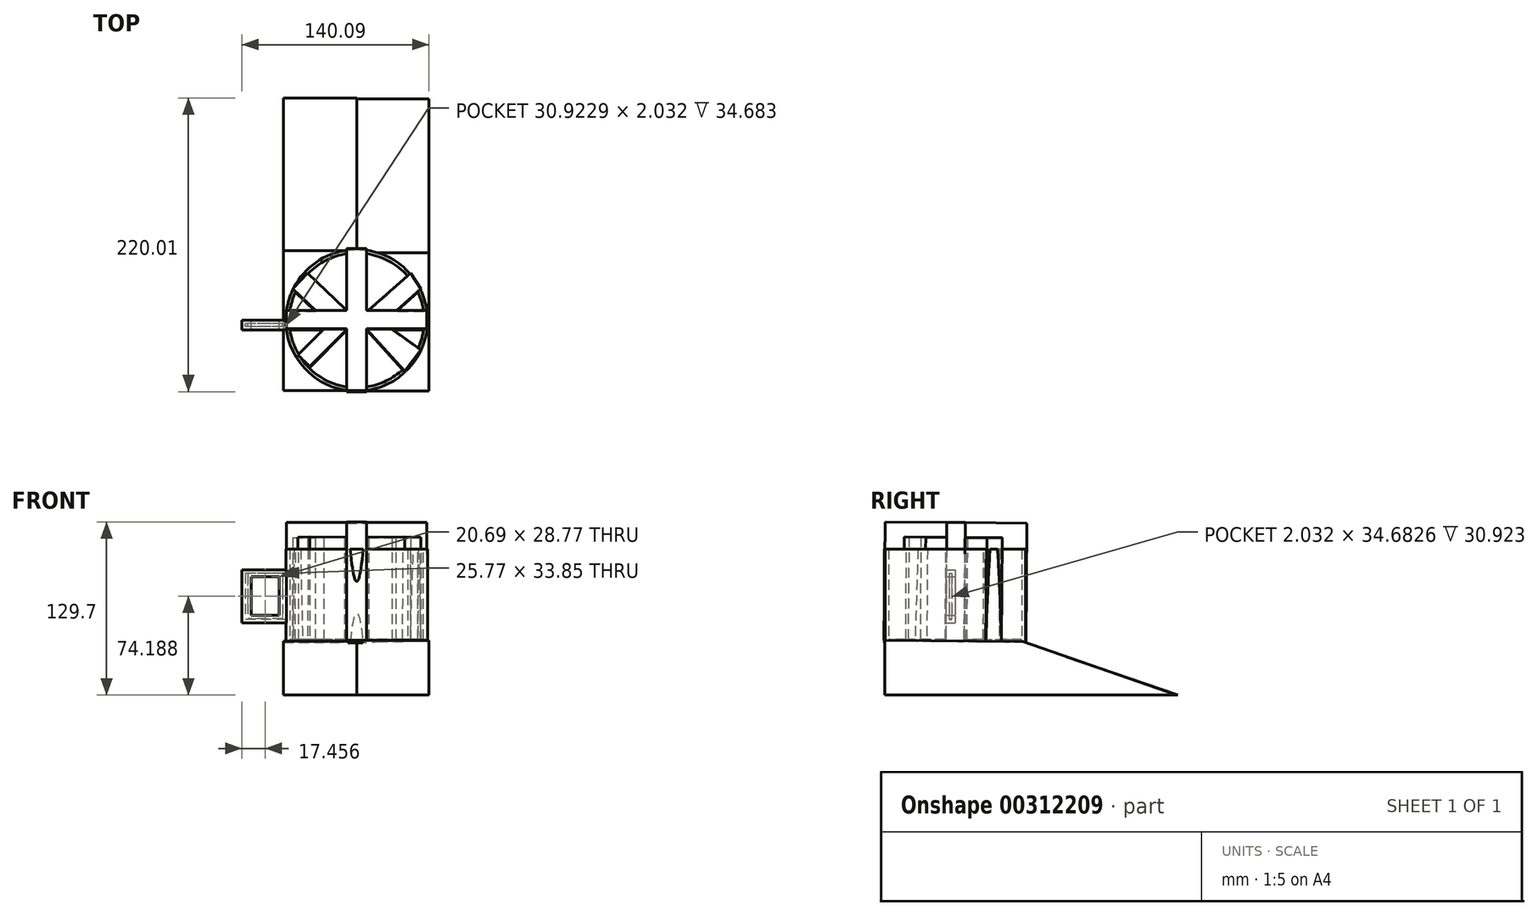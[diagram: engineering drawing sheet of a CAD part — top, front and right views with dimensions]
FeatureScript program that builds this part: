
annotation { "Feature Type Name" : "Feature", "Feature Type Description" : "" }
export const myFeature = defineFeature(function(context is Context, id is Id, definition is map)
    precondition{}
    {
        {
            var Q0;
            Q0=qCreatedBy(makeId("Front.planeOp"),FACE);
            var sketch = newSketch(context, id + "F0", { "sketchPlane" : qUnion([Q0])});
            skLineSegment(sketch, "E0.bottom", {"start": v(0, -34.1) * mm, "end": v(-53.02, -34.1) * mm});
            skLineSegment(sketch, "E0.top", {"start": v(0, 36.04) * mm, "end": v(-53.02, 36.04) * mm});
            skLineSegment(sketch, "E0.left", {"start": v(0, -34.1) * mm, "end": v(0, 36.04) * mm});
            skLineSegment(sketch, "E0.right", {"start": v(-53.02, -34.1) * mm, "end": v(-53.02, 36.04) * mm});
            skSolve(sketch);
        }
        {
            var Q0;
            Q0 = qSketchRegion(id + "F0", true);
            var Q1;
            Q1=sQuery(id+"F0.wireOp",EDGE,"E0.left");
            revolve(context, id + "F1", {"entities" : qUnion([Q0]), "axis" : qUnion([Q1]), "revolveType" : RevolveType.FULL});
        }
        {
            var Q0;
            Q0=qCreatedBy(makeId("Front.planeOp"),FACE);
            var sketch = newSketch(context, id + "F2", { "sketchPlane" : qUnion([Q0])});
            skLineSegment(sketch, "E1.bottom", {"start": v(-52.05, 20.53) * mm, "end": v(-86, 20.53) * mm});
            skLineSegment(sketch, "E1.top", {"start": v(-52.05, -19.24) * mm, "end": v(-86, -19.24) * mm});
            skLineSegment(sketch, "E1.left", {"start": v(-52.05, 20.53) * mm, "end": v(-52.05, -19.24) * mm});
            skLineSegment(sketch, "E1.right", {"start": v(-86, 20.53) * mm, "end": v(-86, -19.24) * mm});
            skLineSegment(sketch, "E2.bottom", {"start": v(-58.19, 15.35) * mm, "end": v(-78.88, 15.35) * mm});
            skLineSegment(sketch, "E2.top", {"start": v(-58.19, -13.42) * mm, "end": v(-78.88, -13.42) * mm});
            skLineSegment(sketch, "E2.left", {"start": v(-58.19, 15.35) * mm, "end": v(-58.19, -13.42) * mm});
            skLineSegment(sketch, "E2.right", {"start": v(-78.88, 15.35) * mm, "end": v(-78.88, -13.42) * mm});
            skSolve(sketch);
        }
        {
            var Q0;
            Q0=makeQuery(id+"F2.imprint","IMPRINT",FACE,{"disambiguationData":[TD([[makeQuery(id+"F2.imprint","IMPRINT",EDGE,{"derivedFrom":sQuery(id+"F2.wireOp",EDGE,"E1.bottom")}),1.0]])]});
            extrude(context, id + "F3", {"entities" : qUnion([Q0]), "operationType" : NewBodyOperationType.ADD, "depth" : 7.11 * mm});
        }
        {
            var Q0;
            Q0=makeQuery(id+"F1.opRevolve","SWEPT_FACE",FACE,{"disambiguationData":[OSD([sQuery(id+"F0.wireOp",EDGE,"E0.top")])]});
            shell(context, id + "F4", {"entities" : qUnion([Q0]), "thickness" : 2.54 * mm});
        }
        {
            var Q0;
            Q0=qCreatedBy(makeId("Right.planeOp"),FACE);
            var sketch = newSketch(context, id + "F5", { "sketchPlane" : qUnion([Q0])});
            skLineSegment(sketch, "E3", {"start": v(-52.84, -32.17) * mm, "end": v(-52.84, -73.22) * mm});
            skLineSegment(sketch, "E4", {"start": v(-52.84, -73.22) * mm, "end": v(165.7, -73.22) * mm});
            skLineSegment(sketch, "E5", {"start": v(165.7, -73.22) * mm, "end": v(50.61, -33.14) * mm});
            skLineSegment(sketch, "E6", {"start": v(50.61, -33.14) * mm, "end": v(-52.84, -32.17) * mm});
            skSolve(sketch);
        }
        {
            var Q0;
            Q0 = qSketchRegion(id + "F5", true);
            extrude(context, id + "F6", {"entities" : qUnion([Q0]), "operationType" : NewBodyOperationType.ADD, "depth" : 54.1 * mm});
        }
        {
            var Q0;
            Q0=qCreatedBy(makeId("Right.planeOp"),FACE);
            var sketch = newSketch(context, id + "F7", { "sketchPlane" : qUnion([Q0])});
            skLineSegment(sketch, "E7", {"start": v(-52.6, -32.81) * mm, "end": v(-52.6, -73.22) * mm});
            skLineSegment(sketch, "E8", {"start": v(-52.6, -73.22) * mm, "end": v(166.58, -73.22) * mm});
            skLineSegment(sketch, "E9", {"start": v(166.58, -73.22) * mm, "end": v(52.14, -33.78) * mm});
            skLineSegment(sketch, "E10", {"start": v(52.14, -33.78) * mm, "end": v(-52.6, -32.81) * mm});
            skSolve(sketch);
        }
        {
            var Q0;
            Q0 = qSketchRegion(id + "F7", true);
            extrude(context, id + "F8", {"entities" : qUnion([Q0]), "operationType" : NewBodyOperationType.ADD, "oppositeDirection" : true, "depth" : 54.86 * mm});
        }
        {
            var Q0;
            Q0=makeQuery(id+"F6.opExtrude","SWEPT_FACE",FACE,{"disambiguationData":[OSD([sQuery(id+"F5.wireOp",EDGE,"E6")])]});
            var sketch = newSketch(context, id + "F9", { "sketchPlane" : qUnion([Q0])});
            skLineSegment(sketch, "E11.bottom", {"start": v(-7.47, -53.12) * mm, "end": v(7.47, -53.12) * mm});
            skLineSegment(sketch, "E11.top", {"start": v(-7.47, 53.12) * mm, "end": v(7.47, 53.12) * mm});
            skLineSegment(sketch, "E11.left", {"start": v(-7.47, -53.12) * mm, "end": v(-7.47, 53.12) * mm});
            skLineSegment(sketch, "E11.right", {"start": v(7.47, -53.12) * mm, "end": v(7.47, 53.12) * mm});
            skPoint(sketch, "E11.middle", {"position": v(0, 0) * mm});
            skLineSegment(sketch, "E12.bottom", {"start": v(52.53, -6.88) * mm, "end": v(-52.53, -6.88) * mm});
            skLineSegment(sketch, "E12.top", {"start": v(52.53, 6.88) * mm, "end": v(-52.53, 6.88) * mm});
            skLineSegment(sketch, "E12.left", {"start": v(52.53, -6.88) * mm, "end": v(52.53, 6.88) * mm});
            skLineSegment(sketch, "E12.right", {"start": v(-52.53, -6.88) * mm, "end": v(-52.53, 6.88) * mm});
            skSolve(sketch);
        }
        {
            var Q0;
            Q0 = qSketchRegion(id + "F9", true);
            extrude(context, id + "F10", {"entities" : qUnion([Q0]), "operationType" : NewBodyOperationType.ADD, "depth" : 88.65 * mm});
        }
        {
            var Q0;
            Q0=makeQuery(id+"F6.opExtrude","SWEPT_FACE",FACE,{"disambiguationData":[OSD([sQuery(id+"F5.wireOp",EDGE,"E6")])]});
            var sketch = newSketch(context, id + "F11", { "sketchPlane" : qUnion([Q0])});
            skLineSegment(sketch, "E13", {"start": v(-6.96, -6.72) * mm, "end": v(-35.28, -35.05) * mm});
            skLineSegment(sketch, "E14", {"start": v(-35.28, -35.05) * mm, "end": v(-44.03, -26.3) * mm});
            skLineSegment(sketch, "E15", {"start": v(-44.03, -26.3) * mm, "end": v(-22.4, -4.66) * mm});
            skLineSegment(sketch, "E16", {"start": v(9.04, 7.2) * mm, "end": v(40.24, 34.83) * mm});
            skLineSegment(sketch, "E17", {"start": v(40.24, 34.83) * mm, "end": v(47.84, 23.16) * mm});
            skLineSegment(sketch, "E18", {"start": v(47.84, 23.16) * mm, "end": v(26.52, 4.1) * mm});
            skLineSegment(sketch, "E19", {"start": v(26.52, 4.1) * mm, "end": v(26.52, -6.88) * mm});
            skLineSegment(sketch, "E20", {"start": v(26.52, -6.88) * mm, "end": v(47.84, -22.55) * mm});
            skLineSegment(sketch, "E21", {"start": v(47.84, -22.55) * mm, "end": v(36.1, -38.53) * mm});
            skLineSegment(sketch, "E22", {"start": v(36.1, -38.53) * mm, "end": v(7.47, -6.88) * mm});
            skLineSegment(sketch, "E23", {"start": v(7.47, -6.88) * mm, "end": v(-9.02, 8.73) * mm});
            skLineSegment(sketch, "E24", {"start": v(-9.02, 8.73) * mm, "end": v(-36.82, 35) * mm});
            skLineSegment(sketch, "E25", {"start": v(-36.82, 35) * mm, "end": v(-48, 23.16) * mm});
            skLineSegment(sketch, "E26", {"start": v(-48, 23.16) * mm, "end": v(-27.81, 4.1) * mm});
            skLineSegment(sketch, "E27", {"start": v(7.47, -6.88) * mm, "end": v(-6.96, -6.72) * mm});
            skLineSegment(sketch, "E28", {"start": v(-22.4, -4.66) * mm, "end": v(-27.81, 4.1) * mm});
            skLineSegment(sketch, "E29", {"start": v(-9.02, 8.73) * mm, "end": v(9.04, 7.2) * mm});
            skLineSegment(sketch, "E30", {"start": v(7.47, -6.88) * mm, "end": v(9.04, 7.2) * mm});
            skSolve(sketch);
        }
        {
            var Q0;
            Q0 = qSketchRegion(id + "F11", true);
            extrude(context, id + "F12", {"entities" : qUnion([Q0]), "operationType" : NewBodyOperationType.ADD, "depth" : 77.47 * mm});
        }
    });
